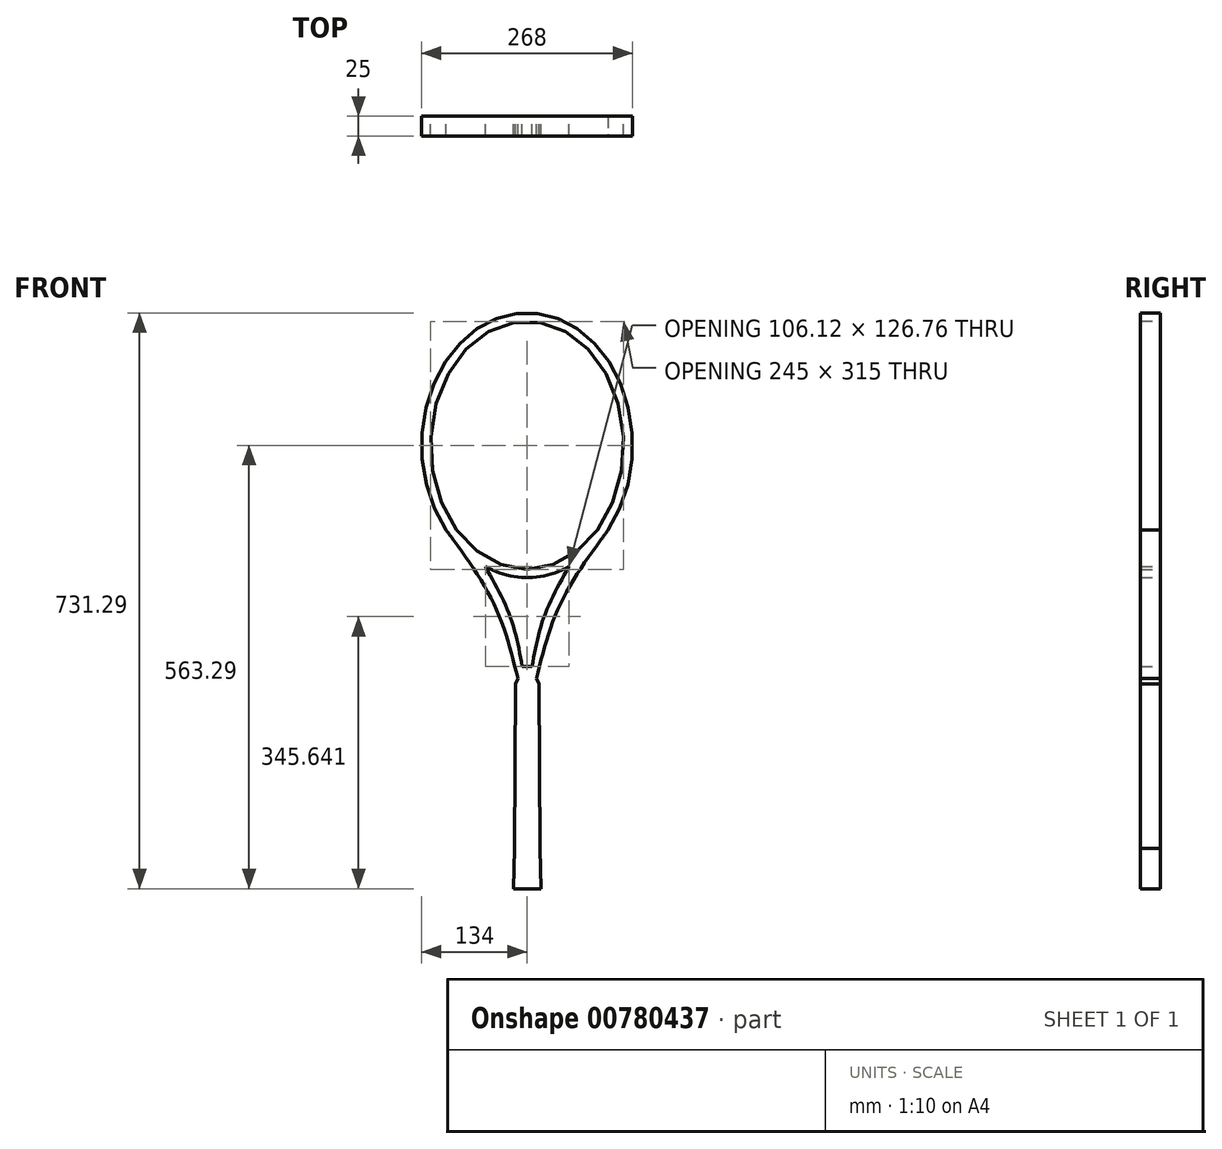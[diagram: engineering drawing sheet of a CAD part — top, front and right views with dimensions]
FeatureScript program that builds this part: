
annotation { "Feature Type Name" : "Feature", "Feature Type Description" : "" }
export const myFeature = defineFeature(function(context is Context, id is Id, definition is map)
    precondition{}
    {
        {
            var Q0;
            Q0=qCreatedBy(makeId("Front.planeOp"),FACE);
            var sketch = newSketch(context, id + "F0", { "sketchPlane" : qUnion([Q0])});
            skEllipse(sketch, "E0", {"center": v(0, 0) * mm, "majorRadius": 168 * mm, "minorRadius": 134 * mm, "majorAxis": v(0, -1)});
            skEllipse(sketch, "E1", {"center": v(0, 0) * mm, "majorRadius": 157.5 * mm, "minorRadius": 122.5 * mm, "majorAxis": v(0, -1)});
            skPoint(sketch, "E2.endSnap0", {"position": v(0, -157.5) * mm});
            skLineSegment(sketch, "E3", {"start": v(0, 232.47) * mm, "end": v(0, -563.3) * mm});
            skLineSegment(sketch, "E4", {"start": v(-15, -303.2) * mm, "end": v(-16.27, -512.11) * mm});
            skLineSegment(sketch, "E5.MirrorCS", {"start": v(15, -303.2) * mm, "end": v(16.27, -512.11) * mm});
            skLineSegment(sketch, "E6", {"start": v(-17.5, -563.3) * mm, "end": v(17.5, -563.3) * mm});
            skLineSegment(sketch, "E7", {"start": v(15, -303.2) * mm, "end": v(-15, -303.2) * mm});
            skLineSegment(sketch, "E8", {"start": v(17.5, -563.3) * mm, "end": v(16.27, -512.11) * mm});
            skLineSegment(sketch, "E9", {"start": v(-16.27, -512.11) * mm, "end": v(-17.5, -563.3) * mm});
            skLineSegment(sketch, "E10", {"start": v(-15, -303.2) * mm, "end": v(-11.77, -296.51) * mm});
            skLineSegment(sketch, "E11", {"start": v(-11.77, -296.51) * mm, "end": v(12.03, -296.51) * mm});
            skLineSegment(sketch, "E12", {"start": v(12.03, -296.51) * mm, "end": v(15, -303.2) * mm});
            skPoint(sketch, "E13", {"position": v(12.03, -296.51) * mm});
            skPoint(sketch, "E14.second.point", {"position": v(0, -255.1) * mm});
            skPoint(sketch, "E15", {"position": v(-102.74, -107.86) * mm});
            skPoint(sketch, "E16.MirrorP", {"position": v(102.74, -107.86) * mm});
            skPoint(sketch, "E17", {"position": v(-42.1, -201.67) * mm});
            skPoint(sketch, "E18.MirrorP", {"position": v(42.1, -201.67) * mm});
            skFitSpline(sketch, "E19", {"points": [v(-11.77, -296.51) * mm, v(-42.1, -201.67) * mm, v(-102.74, -107.86) * mm], "startDerivative": vector(-49, 198.44) * mm, "endDerivative": vector(-132.14, 179.06) * mm});
            skFitSpline(sketch, "E20.MirrorCS", {"points": [v(11.77, -296.51) * mm, v(42.1, -201.67) * mm, v(102.74, -107.86) * mm], "startDerivative": vector(49, 198.44) * mm, "endDerivative": vector(132.14, 179.06) * mm});
            skPoint(sketch, "E21", {"position": v(-53.06, -154.27) * mm});
            skPoint(sketch, "E22.MirrorP", {"position": v(53.06, -154.27) * mm});
            skLineSegment(sketch, "E23", {"start": v(-6.17, -281.03) * mm, "end": v(0, -281.03) * mm});
            skLineSegment(sketch, "E24.MirrorCS", {"start": v(6.17, -281.03) * mm, "end": v(0, -281.03) * mm});
            skPoint(sketch, "E25", {"position": v(-21.56, -217.72) * mm});
            skPoint(sketch, "E26.MirrorP", {"position": v(21.56, -217.72) * mm});
            skFitSpline(sketch, "E27", {"points": [v(-53.06, -154.27) * mm, v(-21.56, -217.72) * mm, v(-6.17, -281.03) * mm], "startDerivative": vector(69.44, -123.02) * mm, "endDerivative": vector(24.02, -130.55) * mm});
            skFitSpline(sketch, "E28.MirrorCS", {"points": [v(53.06, -154.27) * mm, v(21.56, -217.72) * mm, v(6.17, -281.03) * mm], "startDerivative": vector(-69.44, -123.02) * mm, "endDerivative": vector(-24.02, -130.55) * mm});
            skLineSegment(sketch, "E29", {"start": v(-109.74, 69.98) * mm, "end": v(-109.74, -69.98) * mm});
            skLineSegment(sketch, "E30", {"start": v(-96.92, 96.33) * mm, "end": v(-96.92, -96.33) * mm});
            skLineSegment(sketch, "E31", {"start": v(-84.28, 114.3) * mm, "end": v(-84.28, -114.3) * mm});
            skLineSegment(sketch, "E32", {"start": v(-66.83, 132) * mm, "end": v(-66.83, -132) * mm});
            skLineSegment(sketch, "E33", {"start": v(-48.63, 144.56) * mm, "end": v(-48.63, -144.56) * mm});
            skLineSegment(sketch, "E34", {"start": v(-122.5, 0) * mm, "end": v(122.5, 0) * mm});
            skLineSegment(sketch, "E35", {"start": v(-35.35, 150.8) * mm, "end": v(-35.35, -150.8) * mm});
            skLineSegment(sketch, "E36", {"start": v(-20.33, 155.32) * mm, "end": v(-20.33, -155.32) * mm});
            skLineSegment(sketch, "E37", {"start": v(-6.67, 157.27) * mm, "end": v(-6.67, -157.27) * mm});
            skLineSegment(sketch, "E38.MirrorCS", {"start": v(6.67, 157.27) * mm, "end": v(6.67, -157.27) * mm});
            skLineSegment(sketch, "E39.MirrorCS", {"start": v(20.33, 155.32) * mm, "end": v(20.33, -155.32) * mm});
            skLineSegment(sketch, "E40.MirrorCS", {"start": v(35.35, 150.8) * mm, "end": v(35.35, -150.8) * mm});
            skLineSegment(sketch, "E41.MirrorCS", {"start": v(48.63, 144.56) * mm, "end": v(48.63, -144.56) * mm});
            skLineSegment(sketch, "E42.MirrorCS", {"start": v(66.83, 132) * mm, "end": v(66.83, -132) * mm});
            skLineSegment(sketch, "E43.MirrorCS", {"start": v(84.28, 114.3) * mm, "end": v(84.28, -114.3) * mm});
            skLineSegment(sketch, "E44.MirrorCS", {"start": v(96.92, 96.33) * mm, "end": v(96.92, -96.33) * mm});
            skLineSegment(sketch, "E45.MirrorCS", {"start": v(109.74, 69.98) * mm, "end": v(109.74, -69.98) * mm});
            skLineSegment(sketch, "E46", {"start": v(-66.83, 132) * mm, "end": v(66.83, 132) * mm});
            skLineSegment(sketch, "E47", {"start": v(-84.28, 114.3) * mm, "end": v(84.28, 114.3) * mm});
            skLineSegment(sketch, "E48", {"start": v(-96.92, 96.33) * mm, "end": v(96.92, 96.33) * mm});
            skLineSegment(sketch, "E49", {"start": v(-109.74, 69.98) * mm, "end": v(109.74, 69.98) * mm});
            skLineSegment(sketch, "E50", {"start": v(-114.45, 56.16) * mm, "end": v(114.45, 56.16) * mm});
            skLineSegment(sketch, "E51", {"start": v(-118.59, 39.5) * mm, "end": v(118.59, 39.5) * mm});
            skLineSegment(sketch, "E52", {"start": v(-104.75, 81.67) * mm, "end": v(104.75, 81.67) * mm});
            skLineSegment(sketch, "E53", {"start": v(-121.4, 21.14) * mm, "end": v(121.4, 21.14) * mm});
            skLineSegment(sketch, "E54", {"start": v(-122.3, 8.77) * mm, "end": v(122.3, 8.77) * mm});
            skLineSegment(sketch, "E55.MirrorCS", {"start": v(-122.3, -8.77) * mm, "end": v(122.3, -8.77) * mm});
            skLineSegment(sketch, "E56.MirrorCS", {"start": v(-121.4, -21.14) * mm, "end": v(121.4, -21.14) * mm});
            skLineSegment(sketch, "E57.MirrorCS", {"start": v(-118.59, -39.5) * mm, "end": v(118.59, -39.5) * mm});
            skLineSegment(sketch, "E58.MirrorCS", {"start": v(-114.45, -56.16) * mm, "end": v(114.45, -56.16) * mm});
            skLineSegment(sketch, "E59.MirrorCS", {"start": v(-109.74, -69.98) * mm, "end": v(109.74, -69.98) * mm});
            skLineSegment(sketch, "E60.MirrorCS", {"start": v(-104.75, -81.67) * mm, "end": v(104.75, -81.67) * mm});
            skLineSegment(sketch, "E61.MirrorCS", {"start": v(-96.92, -96.33) * mm, "end": v(96.92, -96.33) * mm});
            skLineSegment(sketch, "E62.MirrorCS", {"start": v(-84.28, -114.3) * mm, "end": v(84.28, -114.3) * mm});
            skLineSegment(sketch, "E63.MirrorCS", {"start": v(-66.83, -132) * mm, "end": v(66.83, -132) * mm});
            skSolve(sketch);
        }
        {
            var Q0;
            {var subQ4=sQuery(id+"F0.wireOp",EDGE,"E0");var subQ10=sQuery(id+"F0.wireOp",EDGE,"E19");var subQ11=makeQuery(id+"F0.imprint","INTERSECT",VERTEX,{"disambiguationData":[OD(0.0)],"derivedFrom":[subQ4,subQ10]});Q0=makeQuery(id+"F0.imprint","IMPRINT",FACE,{"disambiguationData":[TD([[makeQuery(id+"F0.imprint","IMPRINT",EDGE,{"disambiguationData":[TD([[subQ11,1.0]])],"derivedFrom":subQ4}),1.0]])]});}
            var Q1;
            {var subQ12=sQuery(id+"F0.wireOp",EDGE,"E0");var subQ27=makeQuery(id+"F0.imprint","INTERSECT",VERTEX,{"derivedFrom":[subQ12,sQuery(id+"F0.wireOp",EDGE,"E28.MirrorCS")]});Q1=makeQuery(id+"F0.imprint","IMPRINT",FACE,{"disambiguationData":[TD([[makeQuery(id+"F0.imprint","IMPRINT",EDGE,{"disambiguationData":[TD([[subQ27,1.0]])],"derivedFrom":subQ12}),1.0]])]});}
            var Q2;
            {var subQ8=sQuery(id+"F0.wireOp",EDGE,"E24.MirrorCS");Q2=makeQuery(id+"F0.imprint","IMPRINT",FACE,{"disambiguationData":[TD([[makeQuery(id+"F0.imprint","IMPRINT",EDGE,{"derivedFrom":subQ8}),1.0]])]});}
            var Q3;
            {var subQ7=sQuery(id+"F0.wireOp",EDGE,"E23");Q3=makeQuery(id+"F0.imprint","IMPRINT",FACE,{"disambiguationData":[TD([[makeQuery(id+"F0.imprint","IMPRINT",EDGE,{"derivedFrom":subQ7}),-1.0]])]});}
            var Q4;
            {var subQ5=sQuery(id+"F0.wireOp",EDGE,"E10");Q4=makeQuery(id+"F0.imprint","IMPRINT",FACE,{"disambiguationData":[TD([[makeQuery(id+"F0.imprint","IMPRINT",EDGE,{"derivedFrom":subQ5}),-1.0]])]});}
            var Q5;
            {var subQ0=sQuery(id+"F0.wireOp",EDGE,"E12");Q5=makeQuery(id+"F0.imprint","IMPRINT",FACE,{"disambiguationData":[TD([[makeQuery(id+"F0.imprint","IMPRINT",EDGE,{"derivedFrom":subQ0}),-1.0]])]});}
            var Q6;
            {var subQ4=sQuery(id+"F0.wireOp",EDGE,"E5.MirrorCS");Q6=makeQuery(id+"F0.imprint","IMPRINT",FACE,{"disambiguationData":[TD([[makeQuery(id+"F0.imprint","IMPRINT",EDGE,{"derivedFrom":subQ4}),-1.0]])]});}
            var Q7;
            {var subQ5=sQuery(id+"F0.wireOp",EDGE,"E4");Q7=makeQuery(id+"F0.imprint","IMPRINT",FACE,{"disambiguationData":[TD([[makeQuery(id+"F0.imprint","IMPRINT",EDGE,{"derivedFrom":subQ5}),1.0]])]});}
            extrude(context, id + "F1", {"entities" : qUnion([Q0, Q1, Q2, Q3, Q4, Q5, Q6, Q7]), "depth" : 25 * mm, "offsetDistance" : 25 * mm});
        }
    });
